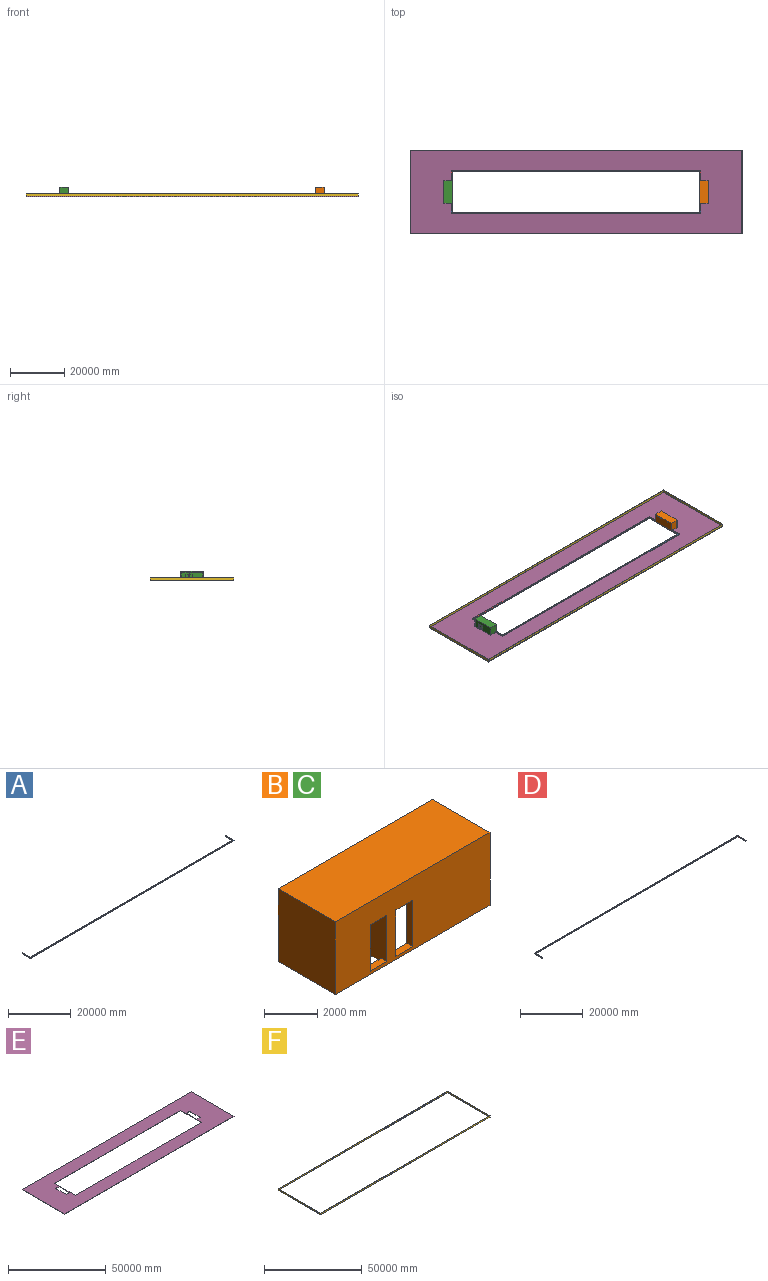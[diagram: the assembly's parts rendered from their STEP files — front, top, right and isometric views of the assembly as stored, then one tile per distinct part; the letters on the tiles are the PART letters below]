
ASSEMBLY  parts=6 mates=5
PART A: 10 faces, bbox 91744.8x3657.6x304.8 mm
  f0: plane 3657.6x304.8mm, normal (-1,0,0), area 1114836.5mm2, adj f2,f5,f6,f9
  f1: plane 3657.6x304.8mm, normal (1,0,0), area 1114836.5mm2, adj f2,f5,f6,f8
  f2: plane 91744.8x3657.6mm, normal (0,0,1), area 30007681.9mm2, adj f0,f1,f3,f4,f5,f7,f8,f9
  f3: plane 3352.8x304.8mm, normal (1,0,0), area 1021933.4mm2, adj f2,f6,f7,f9
  f4: plane 3352.8x304.8mm, normal (-1,0,0), area 1021933.4mm2, adj f2,f6,f7,f8
  f5: plane 91744.8x304.8mm, normal (0,-1,0), area 27963815mm2, adj f0,f1,f2,f6
  f6: plane 91744.8x3657.6mm, normal (0,0,-1), area 30007681.9mm2, adj f0,f1,f3,f4,f5,f7,f8,f9
  f7: plane 91135.2x304.8mm, normal (0,1,0), area 27778009mm2, adj f2,f3,f4,f6
  f8: plane 304.8x304.8mm, normal (0,1,0), area 92903mm2, adj f1,f2,f4,f6
  f9: plane 304.8x304.8mm, normal (0,1,0), area 92903mm2, adj f0,f2,f3,f6
PART B: 23 faces, bbox 8229.6x3048x3352.8 mm
  f0: plane 8229.6x3352.8mm, normal (0,-1,0), area 23798662.1mm2, adj f6,f7,f8,f9,f14,f16,f17,f18
  f1: plane 4876.8x2743.2mm, normal (0,1,0), area 11481267.4mm2, adj f4,f9,f12,f15,f16,f17,f18,f19
  f2: plane 2743.2x2438.4mm, normal (0,-1,0), area 6689018.9mm2, adj f9,f11,f13,f14
  f3: plane 2743.2x2438.4mm, normal (0,1,0), area 4792248.5mm2, adj f9,f11,f13,f14,f20,f21,f22
  f4: plane 4876.8x2438.4mm, normal (0,0,-1), area 11891589.1mm2, adj f1,f10,f12,f15
  f5: plane 8229.6x3352.8mm, normal (0,1,0), area 27592202.9mm2, adj f6,f7,f8,f9
  f6: plane 3352.8x3048mm, normal (-1,0,0), area 10219334.4mm2, adj f0,f5,f8,f9
  f7: plane 3352.8x3048mm, normal (1,0,0), area 10219334.4mm2, adj f0,f5,f8,f9
  f8: plane 8229.6x3048mm, normal (0,0,1), area 25083820.8mm2, adj f0,f5,f6,f7
  f9: plane 8229.6x3048mm, normal (0,0,-1), area 7246437.1mm2, adj f0,f1,f2,f3,f5,f6,f7,f10
  f10: plane 4876.8x2743.2mm, normal (0,-1,0), area 13378037.8mm2, adj f4,f9,f12,f15
  f11: plane 2743.2x2438.4mm, normal (1,0,0), area 6689018.9mm2, adj f2,f3,f9,f13
  f12: plane 2743.2x2438.4mm, normal (-1,0,0), area 6689018.9mm2, adj f1,f4,f9,f10
  f13: plane 2438.4x2438.4mm, normal (0,0,-1), area 5945794.6mm2, adj f2,f3,f11,f14
  f14: plane 2743.2x2743.2mm, normal (-1,0,0), area 7339340.2mm2, adj f0,f2,f3,f9,f13,f20,f21
  f15: plane 2743.2x2438.4mm, normal (1,0,0), area 6689018.9mm2, adj f1,f4,f9,f10
  f16: plane 2133.6x304.8mm, normal (1,0,0), area 650321.3mm2, adj f0,f1,f17,f19
  f17: plane 889x304.8mm, normal (0,0,1), area 270967.2mm2, adj f0,f1,f16,f18
  f18: plane 2133.6x304.8mm, normal (-1,0,0), area 650321.3mm2, adj f0,f1,f17,f19
  f19: plane 889x304.8mm, normal (0,0,-1), area 270967.2mm2, adj f0,f1,f16,f18
  f20: plane 889x304.8mm, normal (0,0,1), area 270967.2mm2, adj f0,f3,f14,f22
  f21: plane 889x304.8mm, normal (0,0,-1), area 270967.2mm2, adj f0,f3,f14,f22
  f22: plane 2133.6x304.8mm, normal (1,0,0), area 650321.3mm2, adj f0,f3,f20,f21
PART C: same geometry as B
PART D: 10 faces, bbox 91744.8x3657.6x304.8 mm
  f0: plane 91744.8x304.8mm, normal (0,1,0), area 27963815mm2, adj f4,f5,f6,f7
  f1: plane 91135.2x304.8mm, normal (0,-1,0), area 27778009mm2, adj f2,f3,f4,f7
  f2: plane 3352.8x304.8mm, normal (-1,0,0), area 1021933.4mm2, adj f1,f4,f7,f8
  f3: plane 3352.8x304.8mm, normal (1,0,0), area 1021933.4mm2, adj f1,f4,f7,f9
  f4: plane 91744.8x3657.6mm, normal (0,0,1), area 30007681.9mm2, adj f0,f1,f2,f3,f5,f6,f8,f9
  f5: plane 3657.6x304.8mm, normal (1,0,0), area 1114836.5mm2, adj f0,f4,f7,f8
  f6: plane 3657.6x304.8mm, normal (-1,0,0), area 1114836.5mm2, adj f0,f4,f7,f9
  f7: plane 91744.8x3657.6mm, normal (0,0,-1), area 30007681.9mm2, adj f0,f1,f2,f3,f5,f6,f8,f9
  f8: plane 304.8x304.8mm, normal (0,-1,0), area 92903mm2, adj f2,f4,f5,f7
  f9: plane 304.8x304.8mm, normal (0,-1,0), area 92903mm2, adj f3,f4,f6,f7
PART E: 18 faces, bbox 122224.8x30784.8x152.4 mm
  f0: plane 122224.8x152.4mm, normal (0,1,0), area 18627059.5mm2, adj f1,f3,f4,f5
  f1: plane 30784.8x152.4mm, normal (-1,0,0), area 4691603.5mm2, adj f0,f2,f4,f5
  f2: plane 122224.8x152.4mm, normal (0,-1,0), area 18627059.5mm2, adj f1,f3,f4,f5
  f3: plane 30784.8x152.4mm, normal (1,0,0), area 4691603.5mm2, adj f0,f2,f4,f5
  f4: plane 122224.8x30784.8mm, normal (0,0,1), area 2364382368mm2, adj f0,f1,f2,f3,f6,f7,f8,f9
  f5: plane 122224.8x30784.8mm, normal (0,0,-1), area 2364382368mm2, adj f0,f1,f2,f3,f6,f7,f8,f9
  f6: plane 91135.2x152.4mm, normal (0,-1,0), area 13889004.5mm2, adj f4,f5,f7,f9
  f7: plane 14935.2x152.4mm, normal (1,0,0), area 2276124.5mm2, adj f4,f5,f6,f8
  f8: plane 91135.2x152.4mm, normal (0,1,0), area 13889004.5mm2, adj f4,f5,f7,f9
  f9: plane 14935.2x152.4mm, normal (-1,0,0), area 2276124.5mm2, adj f4,f5,f6,f8
  f10: plane 2438.4x152.4mm, normal (0,-1,0), area 371612.2mm2, adj f4,f5,f11,f13
  f11: plane 7620x152.4mm, normal (1,0,0), area 1161288mm2, adj f4,f5,f10,f12
  f12: plane 2438.4x152.4mm, normal (0,1,0), area 371612.2mm2, adj f4,f5,f11,f13
  f13: plane 7620x152.4mm, normal (-1,0,0), area 1161288mm2, adj f4,f5,f10,f12
  f14: plane 2438.4x152.4mm, normal (0,-1,0), area 371612.2mm2, adj f4,f5,f15,f17
  f15: plane 7620x152.4mm, normal (1,0,0), area 1161288mm2, adj f4,f5,f14,f16
  f16: plane 2438.4x152.4mm, normal (0,1,0), area 371612.2mm2, adj f4,f5,f15,f17
  f17: plane 7620x152.4mm, normal (-1,0,0), area 1161288mm2, adj f4,f5,f14,f16
PART F: 10 faces, bbox 122224.8x30784.8x914.4 mm
  f0: plane 122224.8x914.4mm, normal (0,1,0), area 111762357.1mm2, adj f1,f3,f4,f5
  f1: plane 30784.8x914.4mm, normal (-1,0,0), area 28149621.1mm2, adj f0,f2,f4,f5
  f2: plane 122224.8x914.4mm, normal (0,-1,0), area 111762357.1mm2, adj f1,f3,f4,f5
  f3: plane 30784.8x914.4mm, normal (1,0,0), area 28149621.1mm2, adj f0,f2,f4,f5
  f4: plane 122224.8x30784.8mm, normal (0,0,1), area 46544423mm2, adj f0,f1,f2,f3,f6,f7,f8,f9
  f5: plane 122224.8x30784.8mm, normal (0,0,-1), area 46544423mm2, adj f0,f1,f2,f3,f6,f7,f8,f9
  f6: plane 121920x914.4mm, normal (0,-1,0), area 111483648mm2, adj f4,f5,f7,f9
  f7: plane 30480x914.4mm, normal (1,0,0), area 27870912mm2, adj f4,f5,f6,f8
  f8: plane 121920x914.4mm, normal (0,1,0), area 111483648mm2, adj f4,f5,f7,f9
  f9: plane 30480x914.4mm, normal (-1,0,0), area 27870912mm2, adj f4,f5,f6,f8
PLACE A t=(0,0,152.4)mm
PLACE B rot(axis=(0,0,1),90deg) t=(47091.6,0,152.4)mm
PLACE C rot(axis=(0,0,-1),90deg) t=(-47091.6,0,152.4)mm
PLACE D t=(0,0,152.4)mm
PLACE E at identity fixed
PLACE F t=(0,0,152.4)mm
MATE fastened A.f6 <-> E.f4  axis (0,0,1) through (45567.6,-7467.6,152.4)mm
MATE fastened B.f9 <-> E.f4  axis (0,0,1) through (48310.8,-3810,152.4)mm
MATE fastened C.f9 <-> E.f4  axis (0,0,1) through (-48310.8,3810,152.4)mm
MATE fastened D.f7 <-> E.f4  axis (0,0,1) through (45567.6,7467.6,152.4)mm
MATE fastened F.f5 <-> E.f4  axis (0,0,1) through (61112.4,-15392.4,152.4)mm
